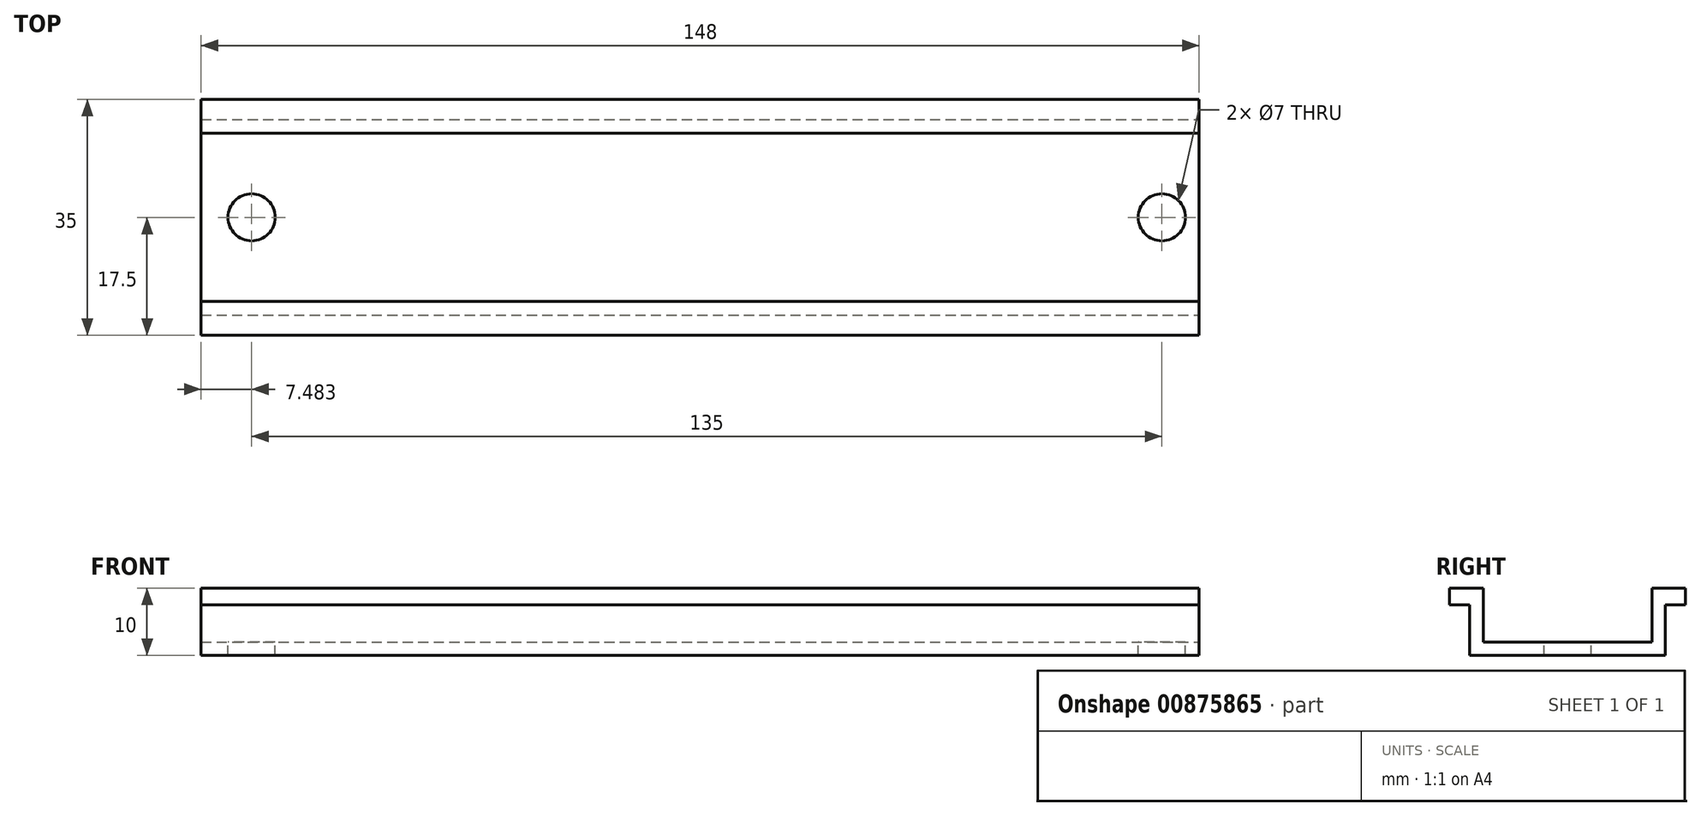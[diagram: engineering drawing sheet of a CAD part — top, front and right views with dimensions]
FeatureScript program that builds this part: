
annotation { "Feature Type Name" : "Feature", "Feature Type Description" : "" }
export const myFeature = defineFeature(function(context is Context, id is Id, definition is map)
    precondition{}
    {
        {
            var Q0;
            Q0=qCreatedBy(makeId("Top.planeOp"),FACE);
            var sketch = newSketch(context, id + "F0", { "sketchPlane" : qUnion([Q0])});
            skLineSegment(sketch, "E0.bottom", {"start": v(-74, 17.5) * mm, "end": v(74, 17.5) * mm});
            skLineSegment(sketch, "E0.top", {"start": v(-74, -17.5) * mm, "end": v(74, -17.5) * mm});
            skLineSegment(sketch, "E0.left", {"start": v(-74, 17.5) * mm, "end": v(-74, -17.5) * mm});
            skLineSegment(sketch, "E0.right", {"start": v(74, 17.5) * mm, "end": v(74, -17.5) * mm});
            skPoint(sketch, "E0.middle", {"position": v(0, 0) * mm});
            skPoint(sketch, "E1", {"position": v(-68, 0) * mm});
            skSolve(sketch);
        }
        {
            var Q0;
            Q0=makeQuery(id+"F0.imprint","IMPRINT",FACE,{"disambiguationData":[TD([[makeQuery(id+"F0.imprint","IMPRINT",EDGE,{"derivedFrom":sQuery(id+"F0.wireOp",EDGE,"E0.bottom")}),-1.0]])]});
            extrude(context, id + "F1", {"entities" : qUnion([Q0]), "depth" : 10 * mm, "offsetDistance" : 25 * mm});
        }
        {
            var Q0;
            Q0=makeQuery(id+"F1.opExtrude","SWEPT_FACE",FACE,{"disambiguationData":[OSD([sQuery(id+"F0.wireOp",EDGE,"E0.right")])]});
            var sketch = newSketch(context, id + "F2", { "sketchPlane" : qUnion([Q0])});
            skLineSegment(sketch, "E2.bottom", {"start": v(-12.5, 10) * mm, "end": v(12.5, 10) * mm});
            skLineSegment(sketch, "E2.top", {"start": v(-12.5, 2) * mm, "end": v(12.5, 2) * mm});
            skLineSegment(sketch, "E2.left", {"start": v(-12.5, 10) * mm, "end": v(-12.5, 2) * mm});
            skLineSegment(sketch, "E2.right", {"start": v(12.5, 10) * mm, "end": v(12.5, 2) * mm});
            skSolve(sketch);
        }
        {
            var Q0;
            Q0=makeQuery(id+"F2.imprint","IMPRINT",FACE,{"disambiguationData":[TD([[makeQuery(id+"F2.imprint","IMPRINT",EDGE,{"derivedFrom":sQuery(id+"F2.wireOp",EDGE,"E2.bottom")}),1.0]])]});
            extrude(context, id + "F3", {"entities" : qUnion([Q0]), "operationType" : NewBodyOperationType.REMOVE, "oppositeDirection" : true, "depth" : 25 * mm, "offsetDistance" : 25 * mm});
        }
        {
            var Q0;
            Q0=makeQuery(id+"F3.boolean.opBoolean","COPY",FACE,{"derivedFrom":makeQuery(id+"F3.opExtrude","CAP_FACE",FACE,{"disambiguationData":[OSD([sQuery(id+"F2.wireOp",EDGE,"E2.bottom"),sQuery(id+"F2.wireOp",EDGE,"E2.top"),sQuery(id+"F2.wireOp",EDGE,"E2.left"),sQuery(id+"F2.wireOp",EDGE,"E2.right")])],"isStart":false})});
            extrude(context, id + "F4", {"entities" : qUnion([Q0]), "operationType" : NewBodyOperationType.REMOVE, "endBound" : BoundingType.THROUGH_ALL, "oppositeDirection" : true, "depth" : 25 * mm, "offsetDistance" : 25 * mm});
        }
        {
            var Q0;
            Q0=makeQuery(id+"F1.opExtrude","SWEPT_FACE",FACE,{"disambiguationData":[OSD([sQuery(id+"F0.wireOp",EDGE,"E0.right")])]});
            var sketch = newSketch(context, id + "F5", { "sketchPlane" : qUnion([Q0])});
            skLineSegment(sketch, "E3.bottom", {"start": v(17.5, 7.5) * mm, "end": v(14.5, 7.5) * mm});
            skLineSegment(sketch, "E3.top", {"start": v(17.5, 0) * mm, "end": v(14.5, 0) * mm});
            skLineSegment(sketch, "E3.left", {"start": v(17.5, 7.5) * mm, "end": v(17.5, 0) * mm});
            skLineSegment(sketch, "E3.right", {"start": v(14.5, 7.5) * mm, "end": v(14.5, 0) * mm});
            skLineSegment(sketch, "E4.MirrorCS", {"start": v(-14.5, 7.5) * mm, "end": v(-14.5, 0) * mm});
            skLineSegment(sketch, "E5.MirrorCS", {"start": v(-17.5, 7.5) * mm, "end": v(-14.5, 7.5) * mm});
            skSolve(sketch);
        }
        {
            var Q0;
            Q0=makeQuery(id+"F5.imprint","IMPRINT",FACE,{"disambiguationData":[TD([[makeQuery(id+"F5.imprint","IMPRINT",EDGE,{"derivedFrom":sQuery(id+"F5.wireOp",EDGE,"E3.bottom")}),1.0]])]});
            var Q1;
            {var subQ0=sQuery(id+"F5.wireOp",EDGE,"E4.MirrorCS");Q1=makeQuery(id+"F5.imprint","IMPRINT",FACE,{"disambiguationData":[TD([[makeQuery(id+"F5.imprint","IMPRINT",EDGE,{"derivedFrom":subQ0}),-1.0]])]});}
            extrude(context, id + "F6", {"entities" : qUnion([Q0, Q1]), "operationType" : NewBodyOperationType.REMOVE, "endBound" : BoundingType.THROUGH_ALL, "oppositeDirection" : true, "depth" : 25 * mm, "offsetDistance" : 25 * mm});
        }
        {
            var Q0;
            {var subQ0=sQuery(id+"F2.wireOp",EDGE,"E2.top");Q0=makeQuery(id+"F4.boolean.opBoolean","MERGE",FACE,{"derivedFrom":[makeQuery(id+"F3.boolean.opBoolean","COPY",FACE,{"derivedFrom":makeQuery(id+"F3.opExtrude","SWEPT_FACE",FACE,{"disambiguationData":[OSD([subQ0])]})})],"fromTools":[makeQuery(id+"F4.opExtrude","SWEPT_FACE",FACE,{"disambiguationData":[OSD([subQ0])]})]});}
            var sketch = newSketch(context, id + "F7", { "sketchPlane" : qUnion([Q0])});
            skPoint(sketch, "E6", {"position": v(-66.52, 0) * mm});
            skPoint(sketch, "E7", {"position": v(68.48, 0) * mm});
            skPoint(sketch, "E8.MirrorP", {"position": v(66.52, 0) * mm});
            skSolve(sketch);
        }
        {
            var Q0;
            Q0=sQuery(id+"F7.wireOp",VERTEX,"E6");
            var Q1;
            Q1=sQuery(id+"F7.wireOp",VERTEX,"E7");
            var Q2;
            Q2=makeQuery(id+"F1.opExtrude","SWEPT_BODY",BODY,{"disambiguationData":[OSD([sQuery(id+"F0.wireOp",EDGE,"E0.bottom"),sQuery(id+"F0.wireOp",EDGE,"E0.top"),sQuery(id+"F0.wireOp",EDGE,"E0.left"),sQuery(id+"F0.wireOp",EDGE,"E0.right")])]});
            hole(context, id + "F8", {"style" : HoleStyle.SIMPLE, "endStyle" : HoleEndStyle.BLIND, "holeDiameter" : 7 * mm, "majorDiameter" : 5 * mm, "holeDepth" : 14.4 * mm, "isTappedThrough" : true, "tappedDepth" : 12 * mm, "tapClearance" : 3, "locations" : qUnion([Q0, Q1]), "scope" : qUnion([Q2])});
        }
    });
